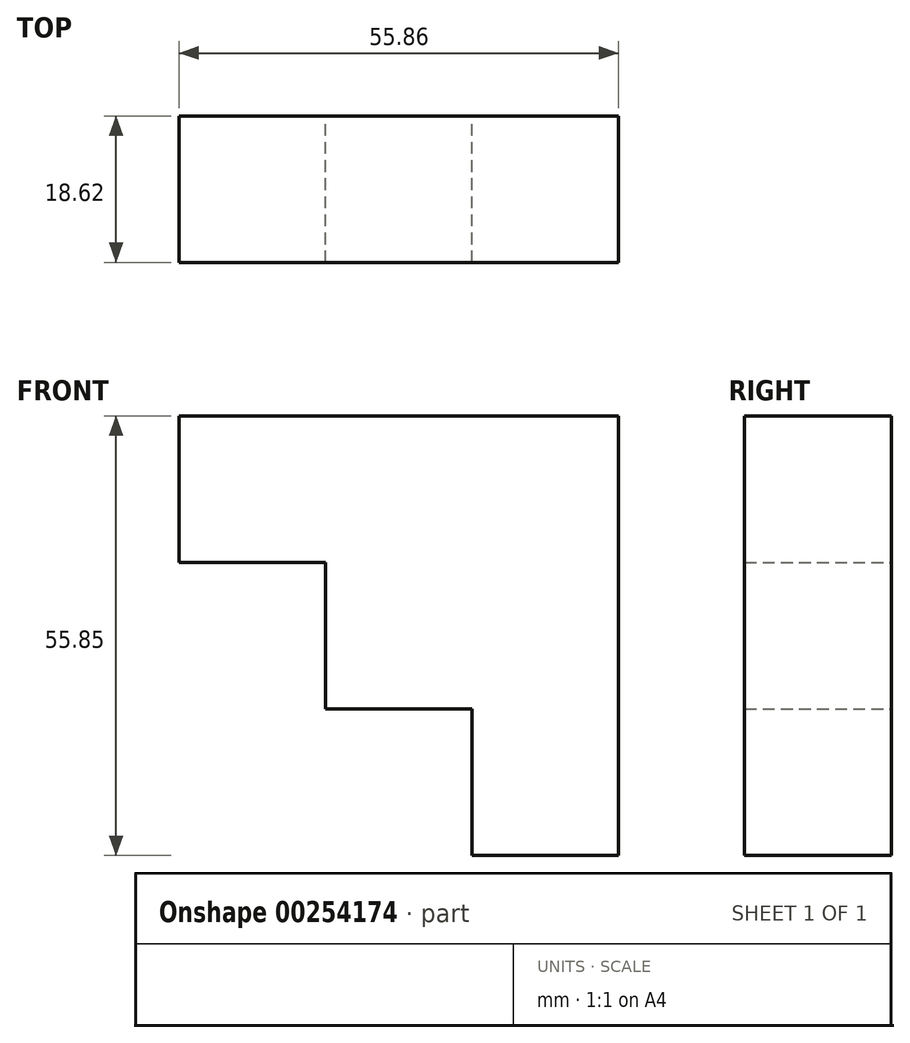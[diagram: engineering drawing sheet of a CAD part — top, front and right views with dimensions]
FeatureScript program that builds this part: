
annotation { "Feature Type Name" : "Feature", "Feature Type Description" : "" }
export const myFeature = defineFeature(function(context is Context, id is Id, definition is map)
    precondition{}
    {
        {
            var Q0;
            Q0=qCreatedBy(makeId("Front.planeOp"),FACE);
            var sketch = newSketch(context, id + "F0", { "sketchPlane" : qUnion([Q0])});
            skLineSegment(sketch, "E0.bottom", {"start": v(-58.67, 23.12) * mm, "end": v(-40.05, 23.12) * mm});
            skLineSegment(sketch, "E0.top", {"start": v(-58.67, 41.73) * mm, "end": v(-40.05, 41.73) * mm});
            skLineSegment(sketch, "E0.left", {"start": v(-58.67, 23.12) * mm, "end": v(-58.67, 41.73) * mm});
            skLineSegment(sketch, "E0.right", {"start": v(-40.05, 23.12) * mm, "end": v(-40.05, 41.73) * mm});
            skLineSegment(sketch, "E1.MirrorCS", {"start": v(-21.43, 41.73) * mm, "end": v(-40.05, 41.73) * mm});
            skLineSegment(sketch, "E2.MirrorCS", {"start": v(-21.43, 23.12) * mm, "end": v(-21.43, 41.73) * mm});
            skLineSegment(sketch, "E3.MirrorCS", {"start": v(-21.43, 23.12) * mm, "end": v(-40.05, 23.12) * mm});
            skLineSegment(sketch, "E4.MirrorCS", {"start": v(-21.43, 41.73) * mm, "end": v(-2.81, 41.73) * mm});
            skLineSegment(sketch, "E5.MirrorCS", {"start": v(-21.43, 23.12) * mm, "end": v(-2.81, 23.12) * mm});
            skLineSegment(sketch, "E6.MirrorCS", {"start": v(-2.81, 23.12) * mm, "end": v(-2.81, 41.73) * mm});
            skLineSegment(sketch, "E7.MirrorCS", {"start": v(-40.05, 23.12) * mm, "end": v(-40.05, 4.5) * mm});
            skLineSegment(sketch, "E8.MirrorCS", {"start": v(-21.43, 23.12) * mm, "end": v(-21.43, 4.5) * mm});
            skLineSegment(sketch, "E9.MirrorCS", {"start": v(-21.43, 4.5) * mm, "end": v(-40.05, 4.5) * mm});
            skLineSegment(sketch, "E10.MirrorCS", {"start": v(-2.81, 23.12) * mm, "end": v(-2.81, 4.5) * mm});
            skLineSegment(sketch, "E11.MirrorCS", {"start": v(-21.43, 4.5) * mm, "end": v(-2.81, 4.5) * mm});
            skLineSegment(sketch, "E12.MirrorCS", {"start": v(-21.43, -14.12) * mm, "end": v(-21.43, 4.5) * mm});
            skLineSegment(sketch, "E13.MirrorCS", {"start": v(-21.43, -14.12) * mm, "end": v(-2.81, -14.12) * mm});
            skLineSegment(sketch, "E14.MirrorCS", {"start": v(-2.81, -14.12) * mm, "end": v(-2.81, 4.5) * mm});
            skSolve(sketch);
        }
        {
            var Q0;
            Q0 = qSketchRegion(id + "F0", true);
            extrude(context, id + "F1", {"entities" : qUnion([Q0]), "depth" : 18.62 * mm});
        }
    });
